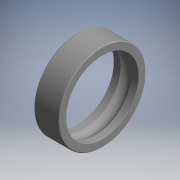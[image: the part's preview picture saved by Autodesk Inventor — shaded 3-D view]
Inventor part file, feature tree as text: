
AUTODESK INVENTOR PART (.ipt)
format: ipt  version: 2017.3 (Build 213256000, 256)  size: 140,288 bytes
history: native  units: mm (DEFAULTED — no unit token found)
features: revolve x1, sketch x1
ambient origin geometry x8: Origin, YZ Plane, XZ Plane, XY Plane, X Axis, Y Axis, Z Axis, Center Point
bodies: Solid1 (feature_tree)
feature tree (2):
  revolve  "Revolution1"  [1 undecoded]
  sketch  "Sketch_1"  dims[d0=360.0deg]
note: 1 required parameter value undecoded (feature->parameter linkage not recoverable at this tier; creation-order binding heuristic only, values carry confidence <= 0.55)
